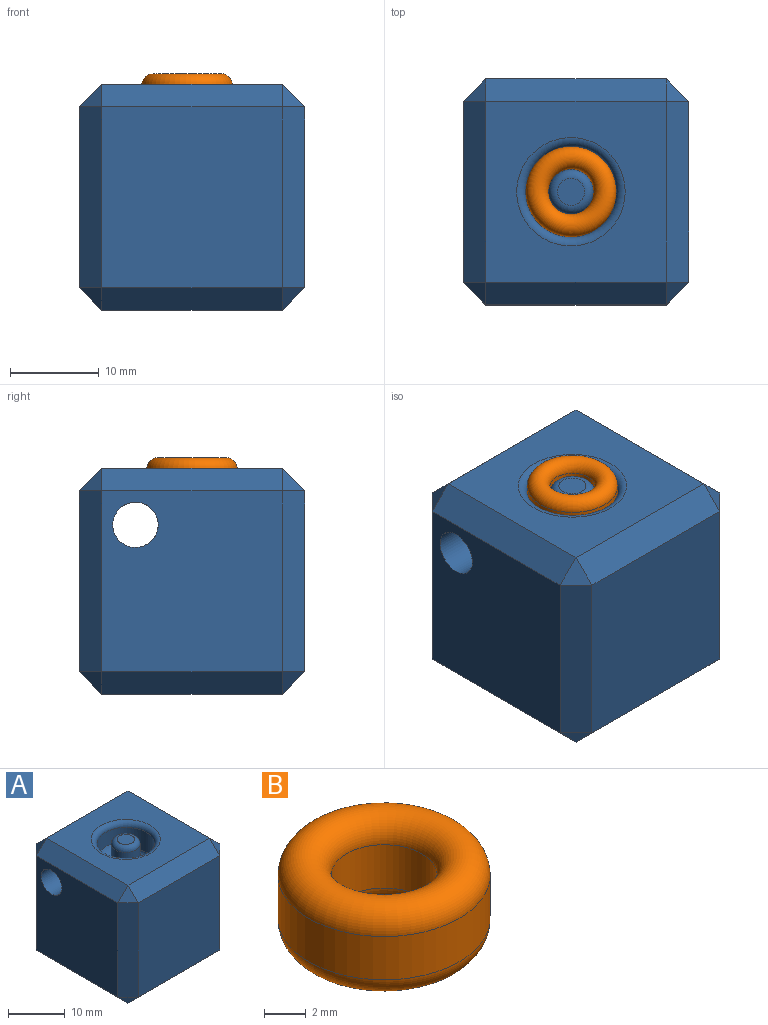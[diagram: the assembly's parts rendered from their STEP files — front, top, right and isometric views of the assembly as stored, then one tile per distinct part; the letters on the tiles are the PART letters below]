
ASSEMBLY  parts=2 mates=1
PART A: 34 faces, bbox 25.4x25.4x25.4 mm
  f0: cylinder r=5.08mm len=10.16mm, axis (0,0,1), area 131.8mm2, adj f2,f12,f33
  f1: plane 8.13x7.86mm, normal (0,0,1), area 31.1mm2, adj f2,f9,f33
  f2: torus R=4.06mm, axis (0,0,1), area 38.1mm2, adj f0,f1,f33
  f3: plane 20.32x20.32mm, normal (0,1,0), area 412.9mm2, adj f19,f20,f28,f29
  f4: plane 20.32x20.32mm, normal (-1,0,0), area 392.4mm2, adj f13,f16,f20,f21,f33
  f5: plane 20.32x20.32mm, normal (0,-1,0), area 412.9mm2, adj f16,f17,f26,f27
  f6: plane 20.32x20.32mm, normal (1,0,0), area 392.4mm2, adj f18,f27,f28,f32,f33
  f7: plane 20.32x20.32mm, normal (0,0,1), area 296.2mm2, adj f12,f13,f17,f18,f19
  f8: plane 20.32x20.32mm, normal (0,0,-1), area 412.9mm2, adj f21,f26,f29,f32
  f9: cylinder r=2.54mm len=5.33mm, axis (0,0,1), area 85.1mm2, adj f1,f11
  f10: plane 3.05x3.05mm, normal (0,0,1), area 7.3mm2, adj f11
  f11: torus R=1.52mm, axis (0,0,1), area 21.8mm2, adj f9,f10
  f12: torus R=6.1mm, axis (0,0,1), area 54.6mm2, adj f0,f7
  f13: plane 20.32x2.54mm, normal (-0.71,0,0.71), area 73mm2, adj f4,f7,f14,f15
  f14: plane 2.54x2.54mm, normal (-0.58,-0.58,0.58), area 5.6mm2, adj f13,f16,f17
  f15: plane 2.54x2.54mm, normal (-0.58,0.58,0.58), area 5.6mm2, adj f13,f19,f20
  f16: plane 20.32x2.54mm, normal (-0.71,-0.71,0), area 73mm2, adj f4,f5,f14,f22
  f17: plane 20.32x2.54mm, normal (0,-0.71,0.71), area 73mm2, adj f5,f7,f14,f23
  f18: plane 20.32x2.54mm, normal (0.71,0,0.71), area 73mm2, adj f6,f7,f23,f24
  f19: plane 20.32x2.54mm, normal (0,0.71,0.71), area 73mm2, adj f3,f7,f15,f24
  f20: plane 20.32x2.54mm, normal (-0.71,0.71,0), area 73mm2, adj f3,f4,f15,f25
  f21: plane 20.32x2.54mm, normal (-0.71,0,-0.71), area 73mm2, adj f4,f8,f22,f25
  f22: plane 2.54x2.54mm, normal (-0.58,-0.58,-0.58), area 5.6mm2, adj f16,f21,f26
  f23: plane 2.54x2.54mm, normal (0.58,-0.58,0.58), area 5.6mm2, adj f17,f18,f27
  f24: plane 2.54x2.54mm, normal (0.58,0.58,0.58), area 5.6mm2, adj f18,f19,f28
  f25: plane 2.54x2.54mm, normal (-0.58,0.58,-0.58), area 5.6mm2, adj f20,f21,f29
  f26: plane 20.32x2.54mm, normal (0,-0.71,-0.71), area 73mm2, adj f5,f8,f22,f30
  f27: plane 20.32x2.54mm, normal (0.71,-0.71,0), area 73mm2, adj f5,f6,f23,f30
  f28: plane 20.32x2.54mm, normal (0.71,0.71,0), area 73mm2, adj f3,f6,f24,f31
  f29: plane 20.32x2.54mm, normal (0,0.71,-0.71), area 73mm2, adj f3,f8,f25,f31
  f30: plane 2.54x2.54mm, normal (0.58,-0.58,-0.58), area 5.6mm2, adj f26,f27,f32
  f31: plane 2.54x2.54mm, normal (0.58,0.58,-0.58), area 5.6mm2, adj f28,f29,f32
  f32: plane 20.32x2.54mm, normal (0.71,0,-0.71), area 73mm2, adj f6,f8,f30,f31
  f33: cylinder r=2.55mm len=25.4mm, axis (1,0,0), area 393.8mm2, adj f0,f1,f2,f4,f6
PART B: 4 faces, bbox 11x11x5.1 mm
  f0: cylinder r=2.54mm len=5.08mm, axis (0,0,-1), area 40.5mm2, adj f2,f3
  f1: cylinder r=5.08mm len=10.16mm, axis (0,0,-1), area 81.1mm2, adj f2,f3
  f2: torus R=3.81mm, axis (0,0,1), area 95.5mm2, adj f0,f1
  f3: torus R=3.81mm, axis (0,0,1), area 95.5mm2, adj f0,f1
PLACE A t=(3.61,14.31,3.39)mm
PLACE B t=(15.74,27.01,24.9)mm
MATE slider A.f0 <-> B.f0  axis (0,0,1) through (15.74,27.01,25.61)mm
